# Revit family: HVAC_HangingSystems_Walraven_Bifix_5000_G2_(BUP1000)
name_source: partatom
category: Mechanical Equipment
revit_build: Autodesk Revit MEP 2016 (Build: 20150220_1215(x64)
units: mm (PartAtom-declared; Revit-internal decimal feet)

## family parameters
Cut with Voids When Loaded = No
Host = Face
OmniClass Number = 23.60.30.11.17
OmniClass Title = Pipework/Ductwork Mechanical Fasteners/Supports
Part Type = Normal
Room Calculation Point = No
Round Connector Dimension = Use Diameter
Shared = No

## types (1)
- std
    Assembly Code = 50
    BIMobject category = Hanging Systems
    BIMobject category code = hvac-hanging-systems
    BIMobject main category = HVAC
    BIMobject main category code = hvac
    Brand url = https://www.walraven.com
    Default Elevation = 1219 mm
    Description = two-screw clamp with lining
    Design country = Netherlands
    Edition number = 0
    IFC Classification = Mechanical Fastener
    IfcDescription = USERDEFINED
    IfcExportAs = IfcMechanicalFastenerType
    IfcExportType = two-screw clamp with lining
    Manufacturer = Walraven
    Manufacturer country = Czech Republic
    Manufacturer name = Walraven
    Material main = Steel
    Model = Bifix 5000 G2 (BUP1000)
    Nominal height = 0 mm  [stored 0 ft]
    Nominal width = 0 mm  [stored 0 ft]
    OmniClass Code = 23-27 43 13
    OmniClass Description = Mechanical Pipe Supports
    Product Guid = c1bfab4b-1c46-42d3-b4e1-9ed86fbf42e8
    Product SKU = bifix-5000-g2-bup1000
    Product data url = https://bimobject.com
    Product family = Pipe Fixing
    Product group = Standard Clamps
    Product url = https://www.walraven.com
    QR code = http://bimobject.com
    RSen_C_code_ETIM = EC010049
    RSen_C_code_ETIM_url = https://prod.etim-international.com
    RSen_C_content_modification_date = 04-02-2019
    RSen_C_content_releasedate = 24-01-2019
    RSen_C_intended_use = hanging systems
    RSen_C_level_of_development = LOD400
    RSen_C_material = steel
    RSen_C_material_01 = EPDM
    RSen_C_material_colour = grey+green
    RSen_C_material_finish = BIS UltraProtect® 1000
    RSen_C_noise_attenuation_norm = sound insulating lining according to DIN 4109
    RSen_C_size_range = Ø16-200mm
    Technical description = https://library.walraven.com
    URL = https://www.walraven.com
    Weight Net (Kg) = 0
    region_index = 1

note: [stored X ft] marks values corroborated as IEEE doubles in the binary element streams (Revit-internal decimal feet)

## geometry (parser evidence)
native form markers: Blend x2, Sweep x9
no freeform markers — native parametric forms only
